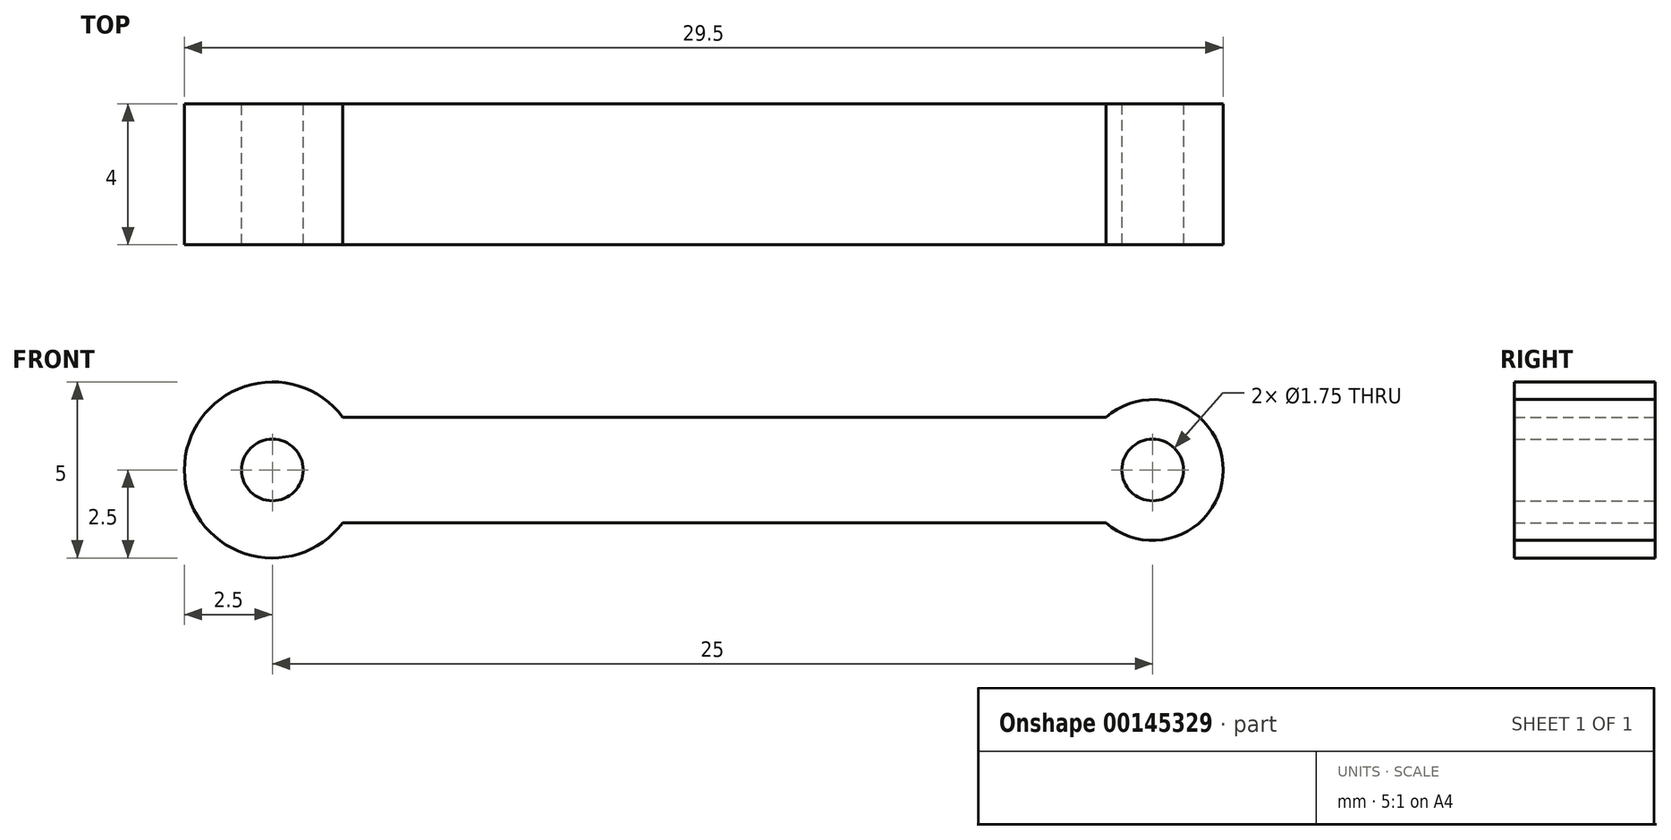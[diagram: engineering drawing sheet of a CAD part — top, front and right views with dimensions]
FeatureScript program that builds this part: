
annotation { "Feature Type Name" : "Feature", "Feature Type Description" : "" }
export const myFeature = defineFeature(function(context is Context, id is Id, definition is map)
    precondition{}
    {
        {
            var Q0;
            Q0=qCreatedBy(makeId("Front.planeOp"),FACE);
            var sketch = newSketch(context, id + "F0", { "sketchPlane" : qUnion([Q0])});
            skCircle(sketch, "E0", {"center": v(-12.5, 0) * mm, "radius": 0.87 * mm});
            skLineSegment(sketch, "E1.bottom", {"start": v(-10.5, -1.5) * mm, "end": v(11.18, -1.5) * mm});
            skLineSegment(sketch, "E1.top", {"start": v(-10.5, 1.5) * mm, "end": v(11.18, 1.5) * mm});
            skArc(sketch, "E2", {"start": v(-10.5, 1.5) * mm, "mid": v(-15, 0) * mm, "end": v(-10.5, -1.5) * mm});
            skCircle(sketch, "E3", {"center": v(12.5, 0) * mm, "radius": 2 * mm});
            skLineSegment(sketch, "E4", {"start": v(11.18, 1.5) * mm, "end": v(11.18, -1.5) * mm});
            skSolve(sketch);
        }
        {
            var Q0;
            Q0 = qSketchRegion(id + "F0", true);
            extrude(context, id + "F1", {"entities" : qUnion([Q0]), "endBound" : BoundingType.SYMMETRIC, "depth" : 4 * mm});
        }
        {
            var Q0;
            Q0=makeQuery(id+"F1.opExtrude","CAP_FACE",FACE,{"disambiguationData":[OSD([sQuery(id+"F0.wireOp",EDGE,"E0"),sQuery(id+"F0.wireOp",EDGE,"E1.bottom"),sQuery(id+"F0.wireOp",EDGE,"E1.top"),sQuery(id+"F0.wireOp",EDGE,"E2"),sQuery(id+"F0.wireOp",EDGE,"E3"),sQuery(id+"F0.wireOp",EDGE,"E4")])],"isStart":false});
            var sketch = newSketch(context, id + "F2", { "sketchPlane" : qUnion([Q0])});
            skCircle(sketch, "E5", {"center": v(12.5, 0) * mm, "radius": 0.88 * mm});
            skSolve(sketch);
        }
        {
            var Q0;
            Q0 = qSketchRegion(id + "F2", true);
            extrude(context, id + "F3", {"entities" : qUnion([Q0]), "operationType" : NewBodyOperationType.REMOVE, "endBound" : BoundingType.THROUGH_ALL, "oppositeDirection" : true, "depth" : 25 * mm});
        }
    });
